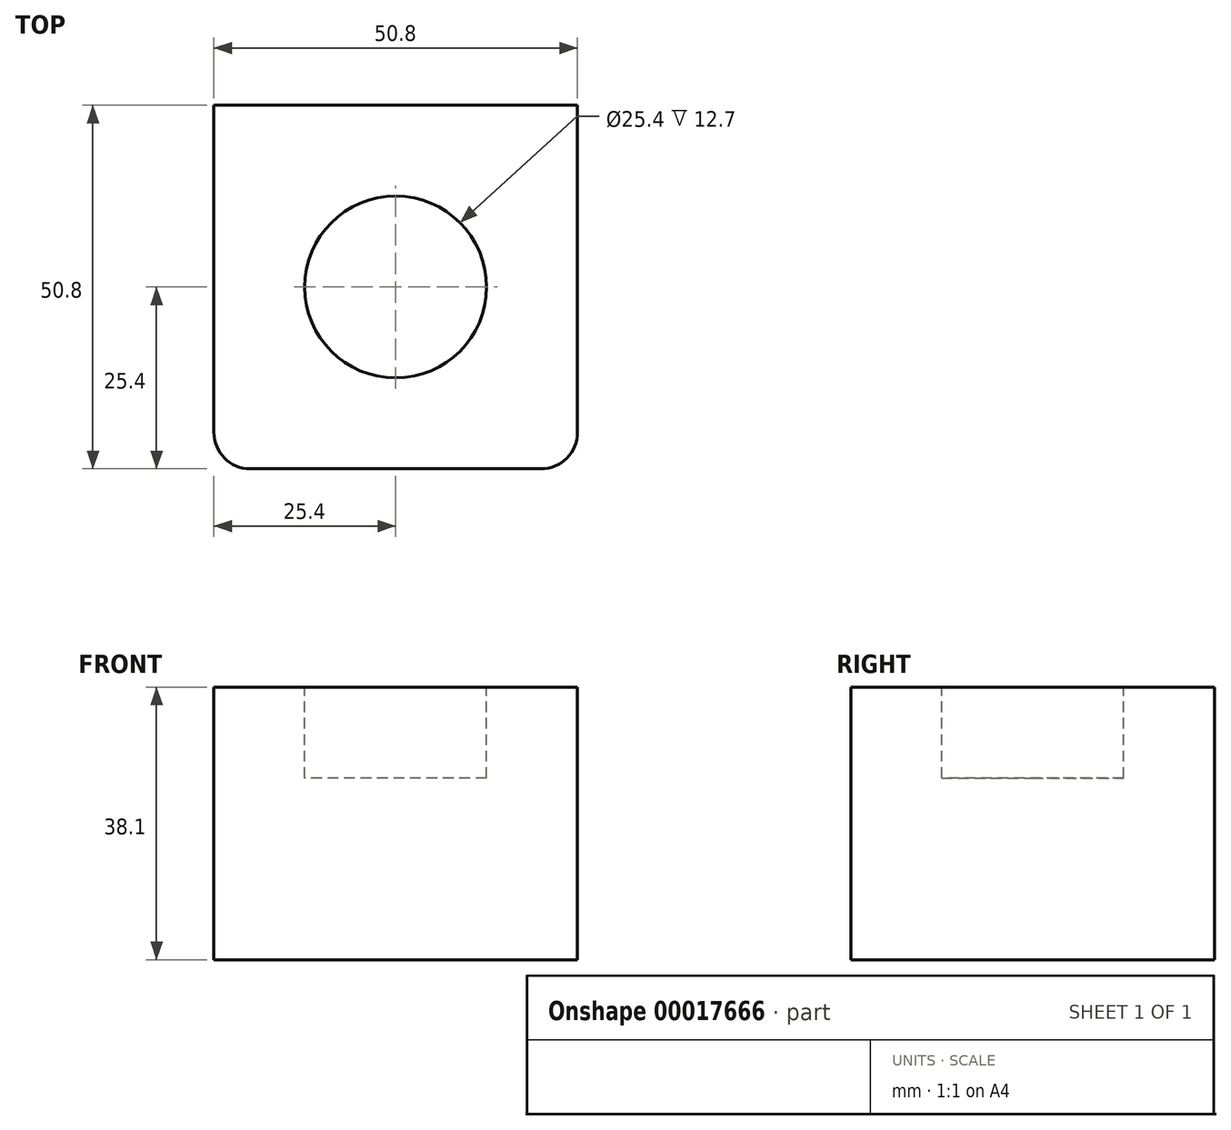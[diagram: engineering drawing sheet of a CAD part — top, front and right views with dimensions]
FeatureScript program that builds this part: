
annotation { "Feature Type Name" : "Feature", "Feature Type Description" : "" }
export const myFeature = defineFeature(function(context is Context, id is Id, definition is map)
    precondition{}
    {
        {
            var Q0;
            Q0=qCreatedBy(makeId("Front.planeOp"),FACE);
            var sketch = newSketch(context, id + "F0", { "sketchPlane" : qUnion([Q0])});
            skLineSegment(sketch, "E0.bottom", {"start": v(0, 38.1) * mm, "end": v(50.8, 38.1) * mm});
            skLineSegment(sketch, "E0.top", {"start": v(0, 0) * mm, "end": v(50.8, 0) * mm});
            skLineSegment(sketch, "E0.left", {"start": v(50.8, 38.1) * mm, "end": v(50.8, 0) * mm});
            skLineSegment(sketch, "E0.right", {"start": v(0, 38.1) * mm, "end": v(0, 0) * mm});
            skSolve(sketch);
        }
        {
            var Q0;
            Q0 = qSketchRegion(id + "F0", true);
            extrude(context, id + "F1", {"entities" : qUnion([Q0]), "depth" : 50.8 * mm});
        }
        {
            var Q0;
            Q0=makeQuery(id+"F1.opExtrude","SWEPT_FACE",FACE,{"disambiguationData":[OSD([sQuery(id+"F0.wireOp",EDGE,"E0.bottom")])]});
            var sketch = newSketch(context, id + "F2", { "sketchPlane" : qUnion([Q0])});
            skCircle(sketch, "E1", {"center": v(25.4, -25.4) * mm, "radius": 12.7 * mm});
            skLineSegment(sketch, "E2", {"start": v(0, 0) * mm, "end": v(50.8, -50.8) * mm, "construction": true});
            skSolve(sketch);
        }
        {
            var Q0;
            Q0 = qSketchRegion(id + "F2", true);
            extrude(context, id + "F3", {"entities" : qUnion([Q0]), "operationType" : NewBodyOperationType.REMOVE, "oppositeDirection" : true, "depth" : 12.7 * mm});
        }
        {
            var Q0;
            Q0=makeQuery(id+"F1.opExtrude","CAP_EDGE",EDGE,{"disambiguationData":[OSD([sQuery(id+"F0.wireOp",EDGE,"E0.right")])],"isStart":false});
            var Q1;
            Q1=makeQuery(id+"F1.opExtrude","CAP_EDGE",EDGE,{"disambiguationData":[OSD([sQuery(id+"F0.wireOp",EDGE,"E0.left")])],"isStart":false});
            fillet(context, id + "F4", {"entities" : qUnion([Q0, Q1]), "radius" : 5.08 * mm, "tangentPropagation" : true, "allowEdgeOverflow" : false});
        }
    });
